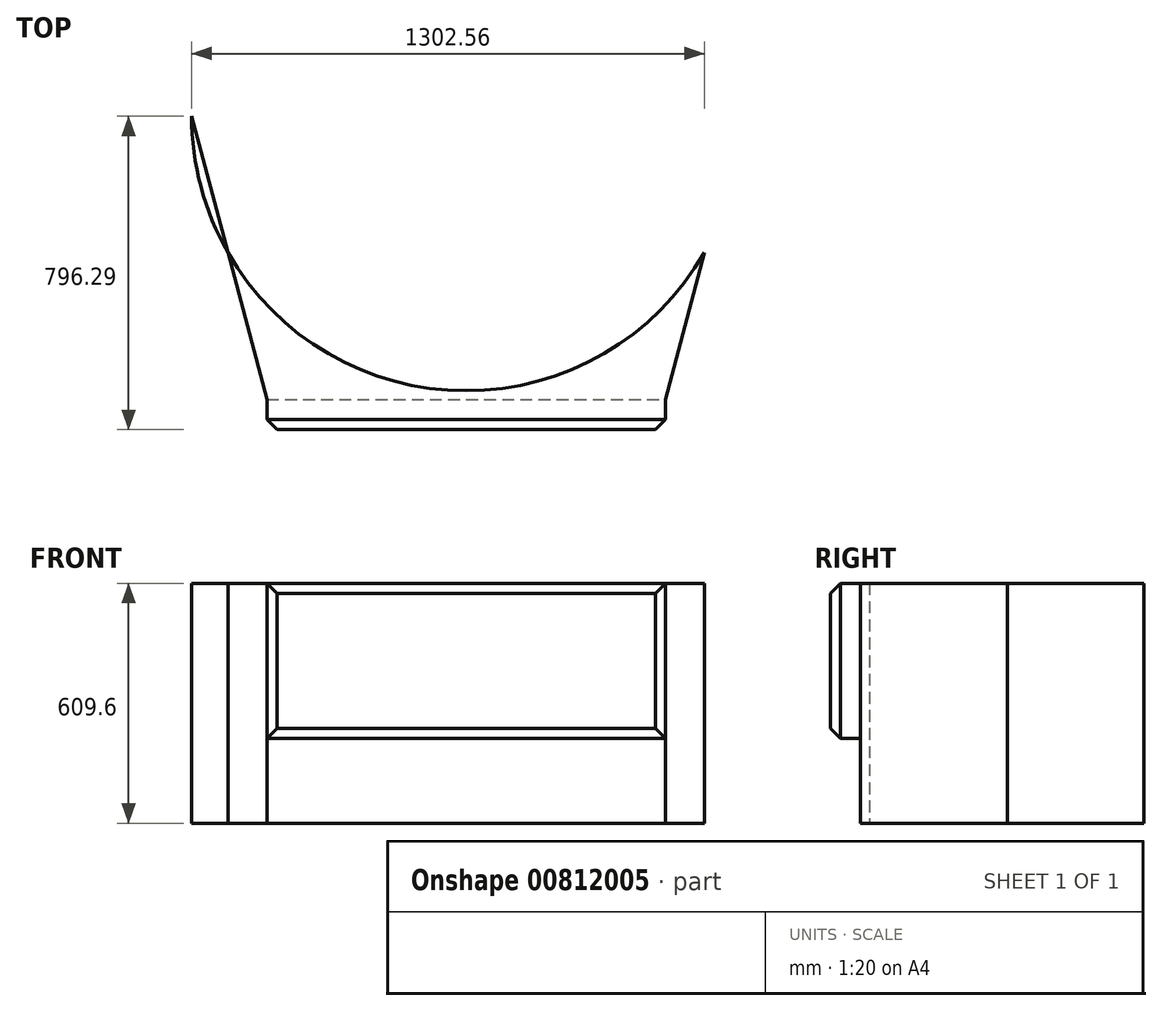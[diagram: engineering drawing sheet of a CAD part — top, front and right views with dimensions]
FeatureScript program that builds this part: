
annotation { "Feature Type Name" : "Feature", "Feature Type Description" : "" }
export const myFeature = defineFeature(function(context is Context, id is Id, definition is map)
    precondition{}
    {
        {
            var Q0;
            Q0=qCreatedBy(makeId("Top.planeOp"),FACE);
            var sketch = newSketch(context, id + "F0", { "sketchPlane" : qUnion([Q0])});
            skCircle(sketch, "E0", {"center": v(0, 0) * mm, "radius": 697.23 * mm});
            skLineSegment(sketch, "E1", {"start": v(-697.23, 0) * mm, "end": v(-505.96, -720.1) * mm});
            skLineSegment(sketch, "E2", {"start": v(0, 0) * mm, "end": v(0, -139.87) * mm});
            skLineSegment(sketch, "E3.MirrorCS", {"start": v(697.23, 0) * mm, "end": v(505.96, -720.1) * mm});
            skLineSegment(sketch, "E4", {"start": v(-505.96, -720.1) * mm, "end": v(505.96, -720.1) * mm});
            skSolve(sketch);
        }
        {
            var Q0;
            {var subQ5=sQuery(id+"F0.wireOp",EDGE,"E4");Q0=makeQuery(id+"F0.imprint","IMPRINT",FACE,{"disambiguationData":[TD([[makeQuery(id+"F0.imprint","IMPRINT",EDGE,{"derivedFrom":subQ5}),1.0]])]});}
            var Q1;
            {var subQ0=sQuery(id+"F0.wireOp",EDGE,"E1");var subQ1=sQuery(id+"F0.wireOp",EDGE,"E0");var subQ2=makeQuery(id+"F0.imprint","INTERSECT",VERTEX,{"disambiguationData":[OD(0.0)],"derivedFrom":[subQ1,subQ0]});Q1=makeQuery(id+"F0.imprint","IMPRINT",FACE,{"disambiguationData":[TD([[makeQuery(id+"F0.imprint","IMPRINT",EDGE,{"disambiguationData":[TD([[subQ2,1.0]])],"derivedFrom":subQ1}),1.0]])]});}
            extrude(context, id + "F1", {"entities" : qUnion([Q0, Q1]), "depth" : 609.6 * mm, "offsetDistance" : 25.4 * mm});
        }
        {
            var Q0;
            Q0=makeQuery(id+"F1.opExtrude","SWEPT_FACE",FACE,{"disambiguationData":[OSD([sQuery(id+"F0.wireOp",EDGE,"E4")])]});
            var sketch = newSketch(context, id + "F2", { "sketchPlane" : qUnion([Q0])});
            skLineSegment(sketch, "E5.bottom", {"start": v(-505.96, 609.6) * mm, "end": v(505.96, 609.6) * mm});
            skLineSegment(sketch, "E5.top", {"start": v(-505.96, 215.6) * mm, "end": v(505.96, 215.6) * mm});
            skLineSegment(sketch, "E5.left", {"start": v(-505.96, 609.6) * mm, "end": v(-505.96, 215.6) * mm});
            skLineSegment(sketch, "E5.right", {"start": v(505.96, 609.6) * mm, "end": v(505.96, 215.6) * mm});
            skSolve(sketch);
        }
        {
            var Q0;
            Q0 = qSketchRegion(id + "F2", true);
            extrude(context, id + "F3", {"entities" : qUnion([Q0]), "operationType" : NewBodyOperationType.ADD, "depth" : 76.2 * mm, "offsetDistance" : 25.4 * mm});
        }
        {
            var Q0;
            Q0=makeQuery(id+"F3.opExtrude","CAP_EDGE",EDGE,{"disambiguationData":[OSD([sQuery(id+"F2.wireOp",EDGE,"E5.bottom")])],"isStart":false});
            var Q1;
            Q1=makeQuery(id+"F3.opExtrude","CAP_EDGE",EDGE,{"disambiguationData":[OSD([sQuery(id+"F2.wireOp",EDGE,"E5.right")])],"isStart":false});
            var Q2;
            Q2=makeQuery(id+"F3.opExtrude","CAP_EDGE",EDGE,{"disambiguationData":[OSD([sQuery(id+"F2.wireOp",EDGE,"E5.top")])],"isStart":false});
            var Q3;
            Q3=makeQuery(id+"F3.opExtrude","CAP_EDGE",EDGE,{"disambiguationData":[OSD([sQuery(id+"F2.wireOp",EDGE,"E5.left")])],"isStart":false});
            chamfer(context, id + "F4", {"entities" : qUnion([Q0, Q1, Q2, Q3]), "width" : 25.4 * mm, "tangentPropagation" : true});
        }
    });
